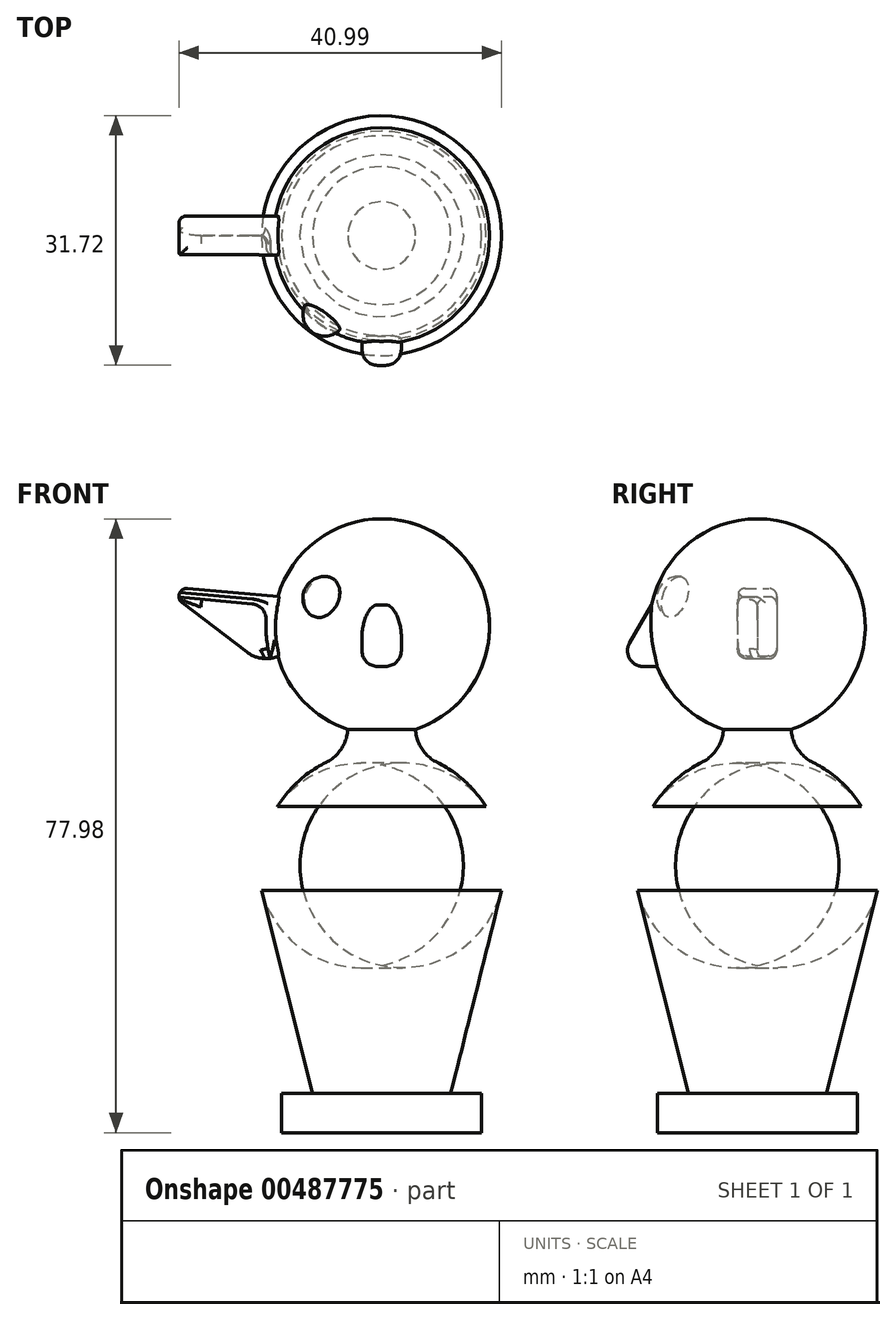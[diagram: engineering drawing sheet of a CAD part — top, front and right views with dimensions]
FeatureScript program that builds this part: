
annotation { "Feature Type Name" : "Feature", "Feature Type Description" : "" }
export const myFeature = defineFeature(function(context is Context, id is Id, definition is map)
    precondition{}
    {
        {
            var Q0;
            Q0=qCreatedBy(makeId("Front.planeOp"),FACE);
            var sketch = newSketch(context, id + "F0", { "sketchPlane" : qUnion([Q0])});
            skLineSegment(sketch, "E0", {"start": v(0, -32.27) * mm, "end": v(-8.6, -32.27) * mm});
            skLineSegment(sketch, "E1", {"start": v(-8.6, -32.27) * mm, "end": v(-16.69, 0) * mm});
            skLineSegment(sketch, "E2", {"start": v(-16.69, 0) * mm, "end": v(-8.6, 11.48) * mm});
            skLineSegment(sketch, "E3", {"start": v(-8.6, 11.48) * mm, "end": v(-4.3, 11.48) * mm});
            skArc(sketch, "E4", {"start": v(0, 41.4) * mm, "mid": v(-13.54, 29.86) * mm, "end": v(-4.3, 14.66) * mm});
            skLineSegment(sketch, "E5", {"start": v(-4.3, 11.48) * mm, "end": v(-4.3, 14.66) * mm});
            skLineSegment(sketch, "E6", {"start": v(0, -32.27) * mm, "end": v(0, 41.4) * mm});
            skPoint(sketch, "E7.orphan", {"position": v(0, 11.48) * mm});
            skSolve(sketch);
        }
        {
            var Q0;
            Q0=makeQuery(id+"F0.imprint","IMPRINT",FACE,{"disambiguationData":[TD([[makeQuery(id+"F0.imprint","IMPRINT",EDGE,{"derivedFrom":sQuery(id+"F0.wireOp",EDGE,"E0")}),-1.0]])]});
            var Q1;
            Q1=sQuery(id+"F0.wireOp",EDGE,"E6");
            revolve(context, id + "F1", {"entities" : qUnion([Q0]), "axis" : qUnion([Q1]), "revolveType" : RevolveType.FULL});
        }
        {
            var Q0;
            Q0=makeQuery(id+"F1.opRevolve","SWEPT_EDGE",EDGE,{"disambiguationData":[OSD([sQuery(id+"F0.wireOp",EDGE,"E1"),sQuery(id+"F0.wireOp",EDGE,"E2")])]});
            fillet(context, id + "F2", {"entities" : qUnion([Q0]), "radius" : 13 * mm, "tangentPropagation" : true, "allowEdgeOverflow" : false});
        }
        {
            var Q0;
            Q0=makeQuery(id+"F1.opRevolve","SWEPT_EDGE",EDGE,{"disambiguationData":[OSD([sQuery(id+"F0.wireOp",EDGE,"E2"),sQuery(id+"F0.wireOp",EDGE,"E3")])]});
            fillet(context, id + "F3", {"entities" : qUnion([Q0]), "radius" : 15 * mm, "tangentPropagation" : true, "allowEdgeOverflow" : false});
        }
        {
            var Q0;
            Q0=makeQuery(id+"F3.opFillet","BLEND_EDGE",EDGE,{"blendedFrom":[makeQuery(id+"F1.opRevolve","SWEPT_EDGE",EDGE,{"disambiguationData":[OSD([sQuery(id+"F0.wireOp",EDGE,"E2"),sQuery(id+"F0.wireOp",EDGE,"E3")])]}),makeQuery(id+"F1.opRevolve","SWEPT_FACE",FACE,{"disambiguationData":[OSD([sQuery(id+"F0.wireOp",EDGE,"E5")])]})],"blendedInto":[makeQuery(id+"F1.opRevolve","SWEPT_FACE",FACE,{"disambiguationData":[OSD([sQuery(id+"F0.wireOp",EDGE,"E5")])]})]});
            fillet(context, id + "F4", {"entities" : qUnion([Q0]), "radius" : 5 * mm, "tangentPropagation" : true, "allowEdgeOverflow" : false});
        }
        {
            var Q0;
            Q0=qCreatedBy(makeId("Front.planeOp"),FACE);
            var sketch = newSketch(context, id + "F5", { "sketchPlane" : qUnion([Q0])});
            skLineSegment(sketch, "E8", {"start": v(-4.64, 30.74) * mm, "end": v(-28.12, 32.86) * mm});
            skLineSegment(sketch, "E9", {"start": v(-28.12, 32.86) * mm, "end": v(-17.08, 24.46) * mm});
            skLineSegment(sketch, "E10", {"start": v(-12.11, 24.56) * mm, "end": v(-4.64, 30.74) * mm});
            skPoint(sketch, "E11.visualSharp", {"position": v(-14.56, 22.53) * mm});
            skArc(sketch, "E11.filletArc", {"start": v(-17.08, 24.46) * mm, "mid": v(-14.58, 23.64) * mm, "end": v(-12.11, 24.56) * mm});
            skSolve(sketch);
        }
        {
            var Q0;
            Q0=makeQuery(id+"F5.imprint","IMPRINT",FACE,{"disambiguationData":[TD([[makeQuery(id+"F5.imprint","IMPRINT",EDGE,{"derivedFrom":sQuery(id+"F5.wireOp",EDGE,"E8")}),1.0]])]});
            extrude(context, id + "F6", {"entities" : qUnion([Q0]), "operationType" : NewBodyOperationType.ADD, "depth" : 2.5 * mm, "hasSecondDirection" : true, "secondDirectionOppositeDirection" : true, "secondDirectionDepth" : 2.5 * mm});
        }
        {
            var Q0;
            Q0=qCreatedBy(makeId("Right.planeOp"),FACE);
            var sketch = newSketch(context, id + "F7", { "sketchPlane" : qUnion([Q0])});
            skLineSegment(sketch, "E12", {"start": v(-12.25, 32.5) * mm, "end": v(-17.95, 22.64) * mm});
            skLineSegment(sketch, "E13", {"start": v(-17.95, 22.64) * mm, "end": v(-10.28, 22.64) * mm});
            skLineSegment(sketch, "E14", {"start": v(-10.28, 22.64) * mm, "end": v(-12.25, 32.5) * mm});
            skSolve(sketch);
        }
        {
            var Q0;
            Q0 = qSketchRegion(id + "F7", true);
            extrude(context, id + "F8", {"entities" : qUnion([Q0]), "operationType" : NewBodyOperationType.ADD, "depth" : 2.5 * mm, "hasSecondDirection" : true, "secondDirectionOppositeDirection" : true, "secondDirectionDepth" : 2.5 * mm});
        }
        {
            var Q0;
            Q0=makeQuery(id+"F8.opExtrude","CAP_EDGE",EDGE,{"disambiguationData":[OSD([sQuery(id+"F7.wireOp",EDGE,"E12")])],"isStart":true});
            var Q1;
            Q1=makeQuery(id+"F8.opExtrude","CAP_EDGE",EDGE,{"disambiguationData":[OSD([sQuery(id+"F7.wireOp",EDGE,"E12")])],"isStart":false});
            var Q2;
            Q2=makeQuery(id+"F8.opExtrude","SWEPT_EDGE",EDGE,{"disambiguationData":[OSD([sQuery(id+"F7.wireOp",EDGE,"E12"),sQuery(id+"F7.wireOp",EDGE,"E13")])]});
            var Q3;
            Q3=makeQuery(id+"F8.opExtrude","CAP_EDGE",EDGE,{"disambiguationData":[OSD([sQuery(id+"F7.wireOp",EDGE,"E13")])],"isStart":true});
            var Q4;
            Q4=makeQuery(id+"F8.opExtrude","CAP_EDGE",EDGE,{"disambiguationData":[OSD([sQuery(id+"F7.wireOp",EDGE,"E13")])],"isStart":false});
            fillet(context, id + "F9", {"entities" : qUnion([Q0, Q1, Q2, Q3, Q4]), "radius" : 2 * mm, "tangentPropagation" : true, "allowEdgeOverflow" : false});
        }
        {
            var Q0;
            Q0=makeQuery(id+"F6.opExtrude","CAP_FACE",FACE,{"disambiguationData":[OSD([sQuery(id+"F5.wireOp",EDGE,"E8"),sQuery(id+"F5.wireOp",EDGE,"E9"),sQuery(id+"F5.wireOp",EDGE,"E10"),sQuery(id+"F5.wireOp",EDGE,"E11.filletArc")])],"isStart":false});
            var sketch = newSketch(context, id + "F10", { "sketchPlane" : qUnion([Q0])});
            skLineSegment(sketch, "E15.0", {"start": v(-14.43, 30.42) * mm, "end": v(-28.23, 31.67) * mm});
            skArc(sketch, "E15.1", {"start": v(-14.43, 30.42) * mm, "mid": v(-14.67, 27.03) * mm, "end": v(-14.13, 23.68) * mm});
            skLineSegment(sketch, "E16", {"start": v(-14.13, 23.68) * mm, "end": v(-14.5, 22.11) * mm});
            skLineSegment(sketch, "E17", {"start": v(-14.5, 22.11) * mm, "end": v(-28.23, 31.67) * mm});
            skSolve(sketch);
        }
        {
            var Q0;
            Q0 = qSketchRegion(id + "F10", true);
            extrude(context, id + "F11", {"entities" : qUnion([Q0]), "operationType" : NewBodyOperationType.REMOVE, "oppositeDirection" : true, "depth" : 2.5 * mm});
        }
        {
            var Q0;
            Q0=makeQuery(id+"F11.boolean.opBoolean","INTERSECT",EDGE,{"derivedFrom":[makeQuery(id+"F6.opExtrude","SWEPT_FACE",FACE,{"disambiguationData":[OSD([sQuery(id+"F5.wireOp",EDGE,"E9")])]}),makeQuery(id+"F11.opExtrude","SWEPT_FACE",FACE,{"disambiguationData":[OSD([sQuery(id+"F10.wireOp",EDGE,"E15.0")])]})]});
            var Q1;
            Q1=makeQuery(id+"F11.boolean.opBoolean","COPY",EDGE,{"derivedFrom":makeQuery(id+"F11.opExtrude","SWEPT_EDGE",EDGE,{"disambiguationData":[OSD([sQuery(id+"F10.wireOp",EDGE,"E15.0"),sQuery(id+"F10.wireOp",EDGE,"E15.1")])]})});
            fillet(context, id + "F12", {"entities" : qUnion([Q0, Q1]), "radius" : 2 * mm, "tangentPropagation" : true, "allowEdgeOverflow" : false});
        }
        {
            var Q0;
            Q0=makeQuery(id+"F11.boolean.opBoolean","INTERSECT",EDGE,{"derivedFrom":[makeQuery(id+"F6.opExtrude","SWEPT_FACE",FACE,{"disambiguationData":[OSD([sQuery(id+"F5.wireOp",EDGE,"E9")])]}),makeQuery(id+"F11.opExtrude","CAP_FACE",FACE,{"disambiguationData":[OSD([sQuery(id+"F10.wireOp",EDGE,"E15.0"),sQuery(id+"F10.wireOp",EDGE,"E15.1"),sQuery(id+"F10.wireOp",EDGE,"E16"),sQuery(id+"F10.wireOp",EDGE,"E17")])],"isStart":false})]});
            var Q1;
            Q1=makeQuery(id+"F6.opExtrude","CAP_EDGE",EDGE,{"disambiguationData":[OSD([sQuery(id+"F5.wireOp",EDGE,"E9")])],"isStart":true});
            var Q2;
            Q2=makeQuery(id+"F6.opExtrude","CAP_EDGE",EDGE,{"disambiguationData":[OSD([sQuery(id+"F5.wireOp",EDGE,"E8")])],"isStart":false});
            var Q3;
            Q3=makeQuery(id+"F6.opExtrude","CAP_EDGE",EDGE,{"disambiguationData":[OSD([sQuery(id+"F5.wireOp",EDGE,"E8")])],"isStart":true});
            var Q4;
            Q4=makeQuery(id+"F6.opExtrude","SWEPT_EDGE",EDGE,{"disambiguationData":[OSD([sQuery(id+"F5.wireOp",EDGE,"E8"),sQuery(id+"F5.wireOp",EDGE,"E9")])]});
            fillet(context, id + "F13", {"entities" : qUnion([Q0, Q1, Q2, Q3, Q4]), "radius" : 1 * mm, "tangentPropagation" : true, "allowEdgeOverflow" : false});
        }
        {
            var Q0;
            Q0=makeQuery(id+"F11.boolean.opBoolean","COPY",EDGE,{"derivedFrom":makeQuery(id+"F11.opExtrude","CAP_EDGE",EDGE,{"disambiguationData":[OSD([sQuery(id+"F10.wireOp",EDGE,"E15.0")])],"isStart":false})});
            var Q1;
            {var subQ0=sQuery(id+"F10.wireOp",EDGE,"E15.1");var subQ1=sQuery(id+"F10.wireOp",EDGE,"E15.0");Q1=makeQuery(id+"F12.opFillet","BLEND_EDGE",EDGE,{"blendedFrom":[makeQuery(id+"F11.boolean.opBoolean","COPY",EDGE,{"derivedFrom":makeQuery(id+"F11.opExtrude","SWEPT_EDGE",EDGE,{"disambiguationData":[OSD([subQ1,subQ0])]})}),makeQuery(id+"F11.boolean.opBoolean","COPY",FACE,{"derivedFrom":makeQuery(id+"F11.opExtrude","CAP_FACE",FACE,{"disambiguationData":[OSD([subQ1,subQ0,sQuery(id+"F10.wireOp",EDGE,"E16"),sQuery(id+"F10.wireOp",EDGE,"E17")])],"isStart":false})})],"blendedInto":[makeQuery(id+"F11.boolean.opBoolean","COPY",FACE,{"derivedFrom":makeQuery(id+"F11.opExtrude","CAP_FACE",FACE,{"disambiguationData":[OSD([subQ1,subQ0,sQuery(id+"F10.wireOp",EDGE,"E16"),sQuery(id+"F10.wireOp",EDGE,"E17")])],"isStart":false})})]});}
            var Q2;
            Q2=makeQuery(id+"F11.boolean.opBoolean","COPY",EDGE,{"derivedFrom":makeQuery(id+"F11.opExtrude","CAP_EDGE",EDGE,{"disambiguationData":[OSD([sQuery(id+"F10.wireOp",EDGE,"E15.1")])],"isStart":false})});
            var Q3;
            Q3=makeQuery(id+"F12.opFillet","BLEND_EDGE",EDGE,{"blendedFrom":[makeQuery(id+"F11.boolean.opBoolean","COPY",EDGE,{"derivedFrom":makeQuery(id+"F11.opExtrude","SWEPT_EDGE",EDGE,{"disambiguationData":[OSD([sQuery(id+"F10.wireOp",EDGE,"E15.0"),sQuery(id+"F10.wireOp",EDGE,"E15.1")])]})}),makeQuery(id+"F6.opExtrude","CAP_FACE",FACE,{"disambiguationData":[OSD([sQuery(id+"F5.wireOp",EDGE,"E8"),sQuery(id+"F5.wireOp",EDGE,"E9"),sQuery(id+"F5.wireOp",EDGE,"E10"),sQuery(id+"F5.wireOp",EDGE,"E11.filletArc")])],"isStart":false})],"blendedInto":[makeQuery(id+"F6.opExtrude","CAP_FACE",FACE,{"disambiguationData":[OSD([sQuery(id+"F5.wireOp",EDGE,"E8"),sQuery(id+"F5.wireOp",EDGE,"E9"),sQuery(id+"F5.wireOp",EDGE,"E10"),sQuery(id+"F5.wireOp",EDGE,"E11.filletArc")])],"isStart":false})]});
            fillet(context, id + "F14", {"entities" : qUnion([Q0, Q1, Q2, Q3]), "radius" : 1 * mm, "tangentPropagation" : true, "allowEdgeOverflow" : false});
        }
        {
            var Q0;
            Q0=makeQuery(id+"F6.opExtrude","CAP_EDGE",EDGE,{"disambiguationData":[OSD([sQuery(id+"F5.wireOp",EDGE,"E11.filletArc")])],"isStart":false});
            fillet(context, id + "F15", {"entities" : qUnion([Q0]), "radius" : 1 * mm, "tangentPropagation" : true, "allowEdgeOverflow" : false});
        }
        {
            var Q0;
            Q0=qCreatedBy(makeId("Front.planeOp"),FACE);
            cPlane(context, id + "F16", {"entities" : qUnion([Q0]), "cplaneType" : CPlaneType.OFFSET, "offset" : 10 * mm, "width" : 150 * mm, "height" : 150 * mm});
        }
        {
            var Q0;
            Q0=qCreatedBy(id+"F16.planeOp",FACE);
            var sketch = newSketch(context, id + "F17", { "sketchPlane" : qUnion([Q0])});
            skArc(sketch, "E18", {"start": v(-7.23, 28.53) * mm, "mid": v(-4.45, 31.3) * mm, "end": v(-7.23, 34.08) * mm});
            skLineSegment(sketch, "E19", {"start": v(-7.23, 34.08) * mm, "end": v(-7.23, 28.53) * mm});
            skSolve(sketch);
        }
        {
            var Q0;
            Q0 = qSketchRegion(id + "F17", true);
            var Q1;
            Q1=sQuery(id+"F17.wireOp",EDGE,"E19");
            revolve(context, id + "F18", {"operationType" : NewBodyOperationType.ADD, "entities" : qUnion([Q0]), "axis" : qUnion([Q1]), "revolveType" : RevolveType.FULL});
        }
        {
            var Q0;
            Q0=qCreatedBy(makeId("Front.planeOp"),FACE);
            var sketch = newSketch(context, id + "F19", { "sketchPlane" : qUnion([Q0])});
            skLineSegment(sketch, "E20.bottom", {"start": v(0, -31.58) * mm, "end": v(-12.7, -31.58) * mm});
            skLineSegment(sketch, "E20.top", {"start": v(0, -36.58) * mm, "end": v(-12.7, -36.58) * mm});
            skLineSegment(sketch, "E20.left", {"start": v(0, -31.58) * mm, "end": v(0, -36.58) * mm});
            skLineSegment(sketch, "E20.right", {"start": v(-12.7, -31.58) * mm, "end": v(-12.7, -36.58) * mm});
            skSolve(sketch);
        }
        {
            var Q0;
            Q0=makeQuery(id+"F19.imprint","IMPRINT",FACE,{"disambiguationData":[TD([[makeQuery(id+"F19.imprint","IMPRINT",EDGE,{"derivedFrom":sQuery(id+"F19.wireOp",EDGE,"E20.bottom")}),1.0]])]});
            var Q1;
            Q1=sQuery(id+"F19.wireOp",EDGE,"E20.left");
            revolve(context, id + "F20", {"operationType" : NewBodyOperationType.ADD, "entities" : qUnion([Q0]), "axis" : qUnion([Q1]), "revolveType" : RevolveType.FULL});
        }
    });
